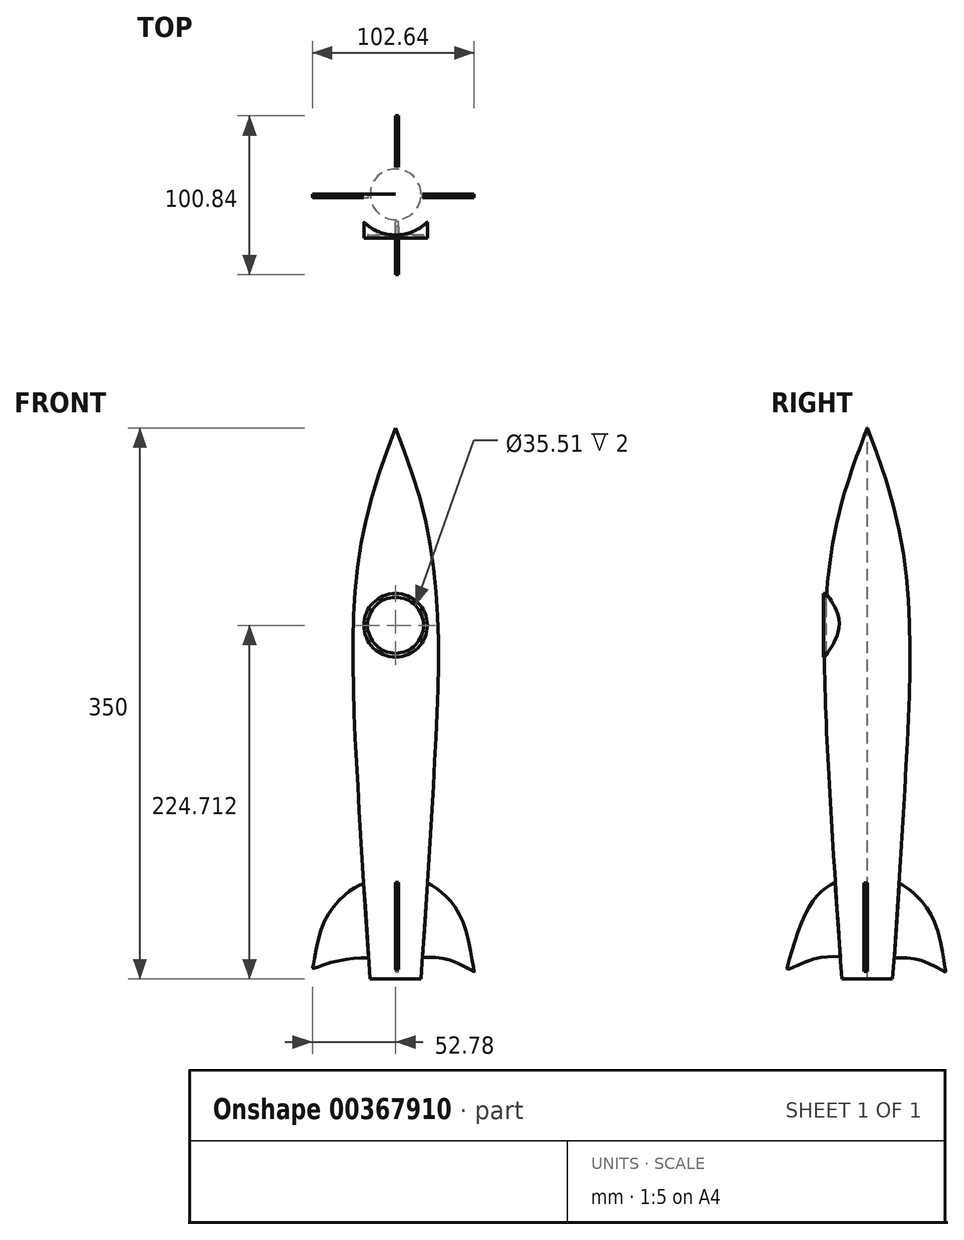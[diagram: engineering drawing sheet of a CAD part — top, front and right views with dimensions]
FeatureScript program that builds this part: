
annotation { "Feature Type Name" : "Feature", "Feature Type Description" : "" }
export const myFeature = defineFeature(function(context is Context, id is Id, definition is map)
    precondition{}
    {
        {
            var Q0;
            Q0=qCreatedBy(makeId("Top.planeOp"),FACE);
            var sketch = newSketch(context, id + "F0", { "sketchPlane" : qUnion([Q0])});
            skCircle(sketch, "E0", {"center": v(0, 0) * mm, "radius": 16.13 * mm});
            skSolve(sketch);
        }
        {
            var Q0;
            Q0=qCreatedBy(makeId("Top.planeOp"),FACE);
            cPlane(context, id + "F1", {"entities" : qUnion([Q0]), "cplaneType" : CPlaneType.OFFSET, "offset" : 150 * mm, "width" : 150 * mm, "height" : 150 * mm});
        }
        {
            var Q0;
            Q0=qCreatedBy(id+"F1.planeOp",FACE);
            var sketch = newSketch(context, id + "F2", { "sketchPlane" : qUnion([Q0])});
            skCircle(sketch, "E1", {"center": v(0, 0) * mm, "radius": 25.46 * mm});
            skSolve(sketch);
        }
        {
            var Q0;
            Q0=qCreatedBy(id+"F1.planeOp",FACE);
            cPlane(context, id + "F3", {"entities" : qUnion([Q0]), "cplaneType" : CPlaneType.OFFSET, "offset" : 150 * mm, "width" : 150 * mm, "height" : 150 * mm});
        }
        {
            var Q0;
            Q0=qCreatedBy(id+"F3.planeOp",FACE);
            var sketch = newSketch(context, id + "F4", { "sketchPlane" : qUnion([Q0])});
            skCircle(sketch, "E2", {"center": v(0, 0) * mm, "radius": 16.86 * mm});
            skSolve(sketch);
        }
        {
            var Q0;
            Q0=qCreatedBy(id+"F3.planeOp",FACE);
            cPlane(context, id + "F5", {"entities" : qUnion([Q0]), "cplaneType" : CPlaneType.OFFSET, "offset" : 50 * mm, "width" : 150 * mm, "height" : 150 * mm});
        }
        {
            var Q0;
            Q0=qCreatedBy(id+"F5.planeOp",FACE);
            var sketch = newSketch(context, id + "F6", { "sketchPlane" : qUnion([Q0])});
            skCircle(sketch, "E3", {"center": v(0, 0) * mm, "radius": 6.03 * mm});
            skSolve(sketch);
        }
        {
            var Q0;
            Q0=makeQuery(id+"F0.imprint","IMPRINT",FACE,{"disambiguationData":[TD([[makeQuery(id+"F0.imprint","IMPRINT",EDGE,{"derivedFrom":sQuery(id+"F0.wireOp",EDGE,"E0")}),1.0]])]});
            var Q1;
            Q1=makeQuery(id+"F2.imprint","IMPRINT",FACE,{"disambiguationData":[TD([[makeQuery(id+"F2.imprint","IMPRINT",EDGE,{"derivedFrom":sQuery(id+"F2.wireOp",EDGE,"E1")}),1.0]])]});
            var Q2;
            Q2=makeQuery(id+"F4.imprint","IMPRINT",FACE,{"disambiguationData":[TD([[makeQuery(id+"F4.imprint","IMPRINT",EDGE,{"derivedFrom":sQuery(id+"F4.wireOp",EDGE,"E2")}),1.0]])]});
            var Q3;
            Q3=sQuery(id+"F6.wireOp",VERTEX,"E3.center");
            loft(context, id + "F7", {"sheetProfilesArray" : [{ "sheetProfileEntities" : qUnion([Q0]) }, { "sheetProfileEntities" : qUnion([Q1]) }, { "sheetProfileEntities" : qUnion([Q2]) }, { "sheetProfileEntities" : qUnion([Q3]) }]});
        }
        {
            var Q0;
            Q0=qCreatedBy(makeId("Front.planeOp"),FACE);
            var sketch = newSketch(context, id + "F8", { "sketchPlane" : qUnion([Q0])});
            skCircle(sketch, "E4", {"center": v(0, 224.71) * mm, "radius": 20.16 * mm});
            skSolve(sketch);
        }
        {
            var Q0;
            Q0 = qSketchRegion(id + "F8", true);
            extrude(context, id + "F9", {"entities" : qUnion([Q0]), "operationType" : NewBodyOperationType.ADD, "depth" : 27.9 * mm});
        }
        {
            var Q0;
            Q0=makeQuery(id+"F9.opExtrude","CAP_FACE",FACE,{"disambiguationData":[OSD([sQuery(id+"F8.wireOp",EDGE,"E4")])],"isStart":false});
            var sketch = newSketch(context, id + "F10", { "sketchPlane" : qUnion([Q0])});
            skCircle(sketch, "E5", {"center": v(0, 224.71) * mm, "radius": 17.75 * mm});
            skSolve(sketch);
        }
        {
            var Q0;
            Q0 = qSketchRegion(id + "F10", true);
            extrude(context, id + "F11", {"entities" : qUnion([Q0]), "operationType" : NewBodyOperationType.REMOVE, "oppositeDirection" : true, "depth" : 2 * mm});
        }
        {
            var Q0;
            Q0=qCreatedBy(makeId("Front.planeOp"),FACE);
            var sketch = newSketch(context, id + "F12", { "sketchPlane" : qUnion([Q0])});
            skLineSegment(sketch, "E6", {"start": v(20.43, 61.21) * mm, "end": v(17.13, 13.8) * mm});
            skFitSpline(sketch, "E7", {"points": [v(20.43, 61.21) * mm, v(30.67, 53.75) * mm, v(43.87, 33.26) * mm, v(49.78, 5.3) * mm, v(49.78, 4.78) * mm, v(36.23, 11.38) * mm, v(17.13, 13.8) * mm], "startDerivative": vector(65.06, -41.4) * mm, "endDerivative": vector(-95.39, -1.07) * mm});
            skSolve(sketch);
        }
        {
            var Q0;
            Q0=qCreatedBy(makeId("Right.planeOp"),FACE);
            var sketch = newSketch(context, id + "F13", { "sketchPlane" : qUnion([Q0])});
            skLineSegment(sketch, "E8", {"start": v(20.45, 60.95) * mm, "end": v(17.15, 13.54) * mm});
            skFitSpline(sketch, "E9", {"points": [v(20.45, 60.95) * mm, v(30.7, 53.48) * mm, v(43.9, 33) * mm, v(49.8, 5.04) * mm, v(49.8, 4.51) * mm, v(36.25, 11.11) * mm, v(17.15, 13.54) * mm], "startDerivative": vector(65.06, -41.4) * mm, "endDerivative": vector(-95.39, -1.07) * mm});
            skSolve(sketch);
        }
        {
            var Q0;
            Q0=qCreatedBy(makeId("Front.planeOp"),FACE);
            var sketch = newSketch(context, id + "F14", { "sketchPlane" : qUnion([Q0])});
            skLineSegment(sketch, "E10", {"start": v(-20.34, 60.8) * mm, "end": v(-17.12, 13.56) * mm});
            skFitSpline(sketch, "E11", {"points": [v(-20.34, 60.8) * mm, v(-30.68, 54.8) * mm, v(-46.9, 32.46) * mm, v(-52.58, 7.67) * mm, v(-52.69, 6.78) * mm, v(-39.9, 10.78) * mm, v(-17.12, 13.56) * mm], "startDerivative": vector(-66.3, -30.77) * mm, "endDerivative": vector(108.9, 4.9) * mm});
            skSolve(sketch);
        }
        {
            var Q0;
            Q0=qCreatedBy(makeId("Right.planeOp"),FACE);
            var sketch = newSketch(context, id + "F15", { "sketchPlane" : qUnion([Q0])});
            skLineSegment(sketch, "E12", {"start": v(-20.53, 61.4) * mm, "end": v(-17.17, 14.24) * mm});
            skFitSpline(sketch, "E13", {"points": [v(-20.53, 61.4) * mm, v(-30.46, 54.54) * mm, v(-42.73, 33.52) * mm, v(-50.76, 7.38) * mm, v(-50.76, 6.21) * mm, v(-35.13, 12.34) * mm, v(-17.17, 14.24) * mm], "startDerivative": vector(-67.16, -36.88) * mm, "endDerivative": vector(90.57, -2.25) * mm});
            skSolve(sketch);
        }
        {
            var Q0;
            Q0=makeQuery(id+"F12.imprint","IMPRINT",FACE,{"disambiguationData":[TD([[makeQuery(id+"F12.imprint","IMPRINT",EDGE,{"derivedFrom":sQuery(id+"F12.wireOp",EDGE,"E6")}),1.0]])]});
            extrude(context, id + "F16", {"entities" : qUnion([Q0]), "depth" : 2 * mm});
        }
        {
            var Q0;
            Q0=makeQuery(id+"F15.imprint","IMPRINT",FACE,{"disambiguationData":[TD([[makeQuery(id+"F15.imprint","IMPRINT",EDGE,{"derivedFrom":sQuery(id+"F15.wireOp",EDGE,"E12")}),-1.0]])]});
            var Q1;
            Q1=makeQuery(id+"F13.imprint","IMPRINT",FACE,{"disambiguationData":[TD([[makeQuery(id+"F13.imprint","IMPRINT",EDGE,{"derivedFrom":sQuery(id+"F13.wireOp",EDGE,"E8")}),1.0]])]});
            extrude(context, id + "F17", {"entities" : qUnion([Q0, Q1]), "depth" : 2 * mm});
        }
        {
            var Q0;
            Q0=makeQuery(id+"F14.imprint","IMPRINT",FACE,{"disambiguationData":[TD([[makeQuery(id+"F14.imprint","IMPRINT",EDGE,{"derivedFrom":sQuery(id+"F14.wireOp",EDGE,"E10")}),-1.0]])]});
            extrude(context, id + "F18", {"entities" : qUnion([Q0]), "depth" : 2 * mm});
        }
        {
            var Q0;
            Q0=makeQuery(id+"F0.imprint","IMPRINT",FACE,{"disambiguationData":[TD([[makeQuery(id+"F0.imprint","IMPRINT",EDGE,{"derivedFrom":sQuery(id+"F0.wireOp",EDGE,"E0")}),1.0]])]});
            var sketch = newSketch(context, id + "F19", { "sketchPlane" : qUnion([Q0])});
            skCircle(sketch, "E14", {"center": v(0, 0) * mm, "radius": 10.96 * mm});
            skSolve(sketch);
        }
        {
            var Q0;
            Q0 = qSketchRegion(id + "F19", true);
            extrude(context, id + "F20", {"entities" : qUnion([Q0]), "operationType" : NewBodyOperationType.REMOVE, "oppositeDirection" : true, "depth" : 5 * mm});
        }
    });
